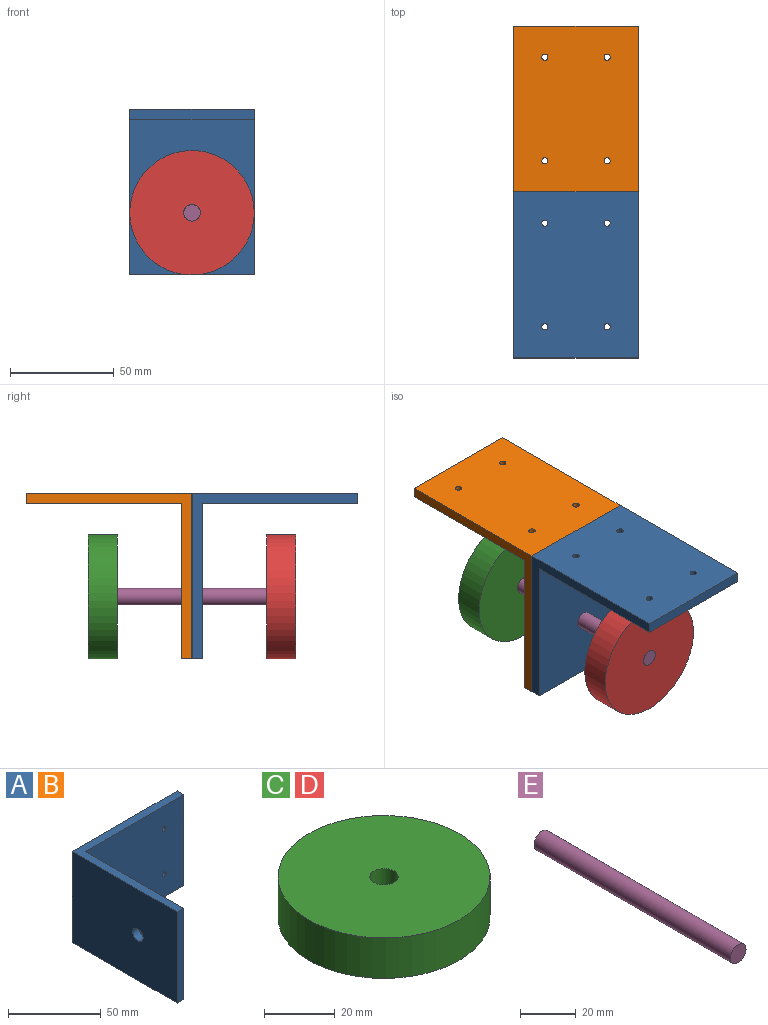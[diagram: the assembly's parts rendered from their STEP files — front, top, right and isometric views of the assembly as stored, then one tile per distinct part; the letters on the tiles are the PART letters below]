
ASSEMBLY  parts=5 mates=4
PART A: 13 faces, bbox 80x80x60 mm
  f0: plane 60x5mm, normal (1,0,0), area 300mm2, adj f1,f5,f6,f7
  f1: plane 80x60mm, normal (0,1,0), area 4771.7mm2, adj f0,f2,f6,f7,f9,f10,f11,f12
  f2: plane 80x60mm, normal (-1,0,0), area 4749.7mm2, adj f1,f3,f6,f7,f8
  f3: plane 60x5mm, normal (0,-1,0), area 300mm2, adj f2,f4,f6,f7
  f4: plane 75x60mm, normal (1,0,0), area 4449.7mm2, adj f3,f5,f6,f7,f8
  f5: plane 75x60mm, normal (0,-1,0), area 4471.7mm2, adj f0,f4,f6,f7,f9,f10,f11,f12
  f6: plane 80x80mm, normal (0,0,1), area 775mm2, adj f0,f1,f2,f3,f4,f5
  f7: plane 80x80mm, normal (0,0,-1), area 775mm2, adj f0,f1,f2,f3,f4,f5
  f8: cylinder r=4mm len=8mm, axis (-1,0,0), area 125.7mm2, adj f2,f4
  f9: cylinder r=1.5mm len=5mm, axis (0,1,0), area 47.1mm2, adj f1,f5
  f10: cylinder r=1.5mm len=5mm, axis (0,1,0), area 47.1mm2, adj f1,f5
  f11: cylinder r=1.5mm len=5mm, axis (0,1,0), area 47.1mm2, adj f1,f5
  f12: cylinder r=1.5mm len=5mm, axis (0,1,0), area 47.1mm2, adj f1,f5
PART B: same geometry as A
PART C: 4 faces, bbox 60x60x14 mm
  f0: cylinder r=4mm len=14mm, axis (0,0,-1), area 351.9mm2, adj f2,f3
  f1: cylinder r=30mm len=60mm, axis (0,0,-1), area 2638.9mm2, adj f2,f3
  f2: plane 60x60mm, normal (0,0,1), area 2777.2mm2, adj f0,f1
  f3: plane 60x60mm, normal (0,0,-1), area 2777.2mm2, adj f0,f1
PART D: same geometry as C
PART E: 3 faces, bbox 8x100x8 mm
  f0: plane 8x8mm, normal (0,1,0), area 50.3mm2, adj f2
  f1: plane 8x8mm, normal (0,-1,0), area 50.3mm2, adj f2
  f2: cylinder r=4mm len=100mm, axis (0,-1,0), area 2513.3mm2, adj f0,f1
PLACE A rot(axis=(0.58,-0.58,-0.58),120deg) t=(-101.16,71.65,-413.37)mm
PLACE B rot(axis=(0.58,0.58,0.58),120deg) t=(-161.16,2.46,-413.37)mm
PLACE C rot(axis=(-1,0,0),90deg) t=(-72.24,73.05,-388.96)mm
PLACE D rot(axis=(-1,0,0),90deg) t=(-72.24,-12.95,-388.96)mm
PLACE E t=(-131.16,14.55,-391.2)mm
MATE fastened C.f0 <-> E.f2  axis (0,1,0) through (-131.16,87.05,-387.2)mm
MATE fastened A.f8 <-> E.f2  axis (0,1,0) through (-131.16,37.05,-387.2)mm
MATE fastened B.f8 <-> E.f2  axis (0,-1,0) through (-131.16,37.05,-387.2)mm
MATE fastened D.f0 <-> E.f2  axis (0,-1,0) through (-131.16,-12.95,-387.2)mm
